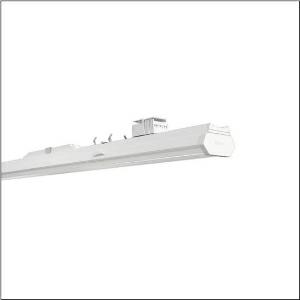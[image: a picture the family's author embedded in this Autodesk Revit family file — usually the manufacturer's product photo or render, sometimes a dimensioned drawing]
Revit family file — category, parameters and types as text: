
# Revit family: licross_11_protected_ho_51td13dn4f5s
name_source: partatom
category: Lighting Fixtures
units: mm (PartAtom-declared; Revit-internal decimal feet)

## family parameters
Cut with Voids When Loaded = No
Host = Face
Light Source = No
Part Type = Normal
Room Calculation Point = No
Round Connector Dimension = Use Diameter
Shared = No

## types (1)
- --- (1 x LED, 15550 lm, 87.3 W, 4000K)
    Apparent Load = 87 VA
    CIE Flux Codes = 89 96 99 100 99
    Color Rendering = 80
    Color Temperature = 4000K
    Default Elevation = 1800 mm
    Description = Licross 11 Protected HO, luminaire insert, of sheet steel, galvanised, coil coated, white, length: 1.500mm, width: 90mm, height: 101mm, LED rated luminous flux: 15.550lm, light colour: 840, SDCM (Standard Deviation of Colour Matching)MacAdam ≤ 2 SDCM (initial), control gear: DALI 2, with plug, 5-pole, with phase selection, mains connection: 220..240V, AC, 50/60Hz, rated input power: 87W, internal wiring halogen-free, primary light control with lens, of plastic, primary optical cover: cover, of PMMA, light emission: direct distribution, primary light characteristic: symmetric, protection rating (complete): IP54, insulation class (complete): insulation class I (protective earthing), certification: CE, ENEC, VDE, UKCA, protection symbol: D if used in an environment with non-conductive dust loads with corresponding accessories, impact resistance: IK06, permissible ambient temperature for indoor applications: -25..+30°C, corresponds to IFS (International Featured Standards) requirements for safety and quality in the food industry, reducing of maximum allowable ambient temperature of 5°C with ceiling mounting, LABS conformity tested according to VDMA 24364:2018-05, The light source and the operating device comply with the requirements of the Ecodesign Regulation (EU) 2019/2020 and are replaceable in accordance with this regulation, packaging unit: 1 piece
    Height = 92 mm
    Lamp = 1 x LED
    Lamp Light Flux = 15550 lm
    Lamp Power = 87.3 W
    Lamp count = 1
    Length = 1500 mm
    Luminous efficacy = 178 lm/W
    Manufacturer = Siteco
    ModVariant = No
    Model = 51TD13DN4F5S
    Mounting Place = Ceiling
    Mounting Type = Pendant
    Number of Poles = 1
    OnlyDefault = Yes
    Power Factor = 1
    Product Name = Licross 11 Protected HO
    Product group = luminaire insert | ceiling pendant
    ProductGroupID = 901
    Protection Class = Protection class I
    Protection Degree = IP 54
    RLX_Detail_Level = 1
    RLX_Emergency_Light_Flux = 0 lm
    RLX_Emergency_Type = 0
    RLX_Emergency_Type_DB = No
    RlxData = <blob elided: 24653 chars, md5=03144af1>
    Socket = socket
    Standby Power = 0 W
    System Light Flux = 15550 lm
    System Power = 87 W
    Type Comments = factory setting: luminous flux: 100 % | dim-lin: 254 | 589 mA
    Type Image = l_1256145.jpg
    URL = http://relux.com
    VarID = @adj_102473
    Voltage = 0 V
    Weight = 0.00 kg
    Width = 88 mm

## geometry (parser evidence)
native form markers: Blend x4, Sweep x10
no freeform markers — native parametric forms only
